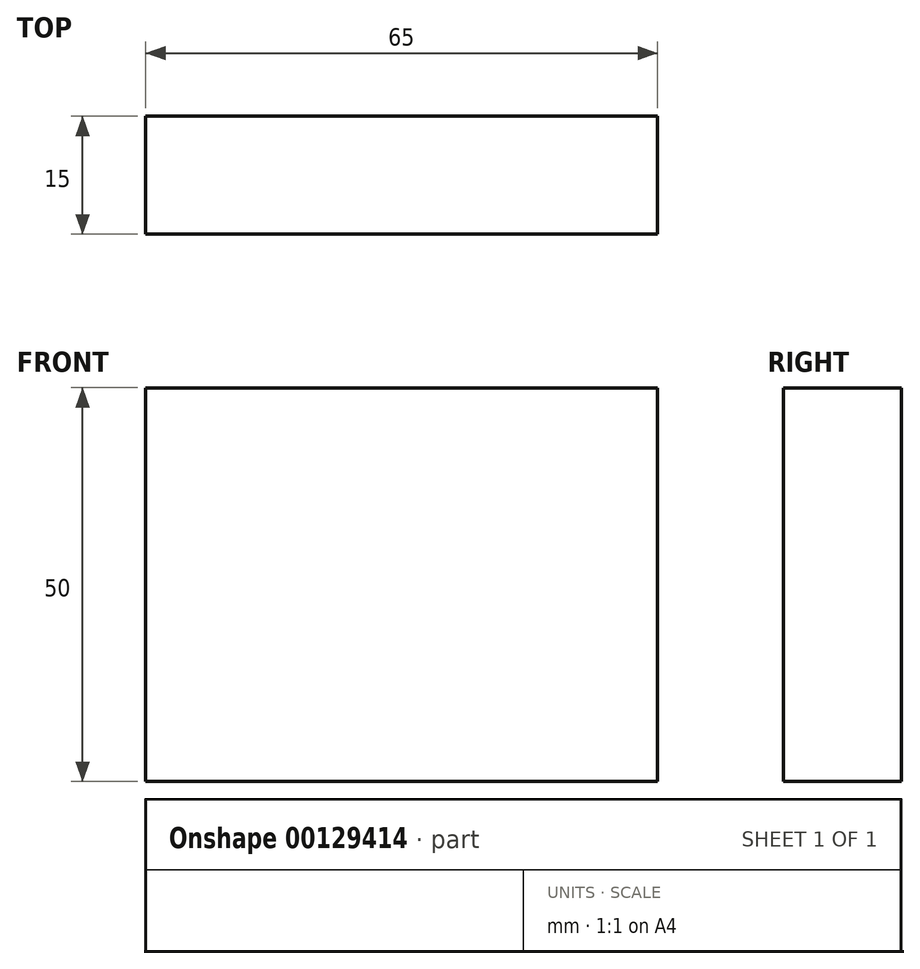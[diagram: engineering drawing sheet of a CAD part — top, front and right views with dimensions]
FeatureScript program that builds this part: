
annotation { "Feature Type Name" : "Feature", "Feature Type Description" : "" }
export const myFeature = defineFeature(function(context is Context, id is Id, definition is map)
    precondition{}
    {
        {
            var Q0;
            Q0=qCreatedBy(makeId("Front.planeOp"),FACE);
            var sketch = newSketch(context, id + "F0", { "sketchPlane" : qUnion([Q0])});
            skLineSegment(sketch, "E0.bottom", {"start": v(-39.52, 26.83) * mm, "end": v(25.48, 26.83) * mm});
            skLineSegment(sketch, "E0.top", {"start": v(-39.52, -23.17) * mm, "end": v(25.48, -23.17) * mm});
            skLineSegment(sketch, "E0.left", {"start": v(-39.52, 26.83) * mm, "end": v(-39.52, -23.17) * mm});
            skLineSegment(sketch, "E0.right", {"start": v(25.48, 26.83) * mm, "end": v(25.48, -23.17) * mm});
            skSolve(sketch);
        }
        {
            var Q0;
            Q0 = qSketchRegion(id + "F0", true);
            extrude(context, id + "F1", {"entities" : qUnion([Q0]), "depth" : 15 * mm});
        }
    });
